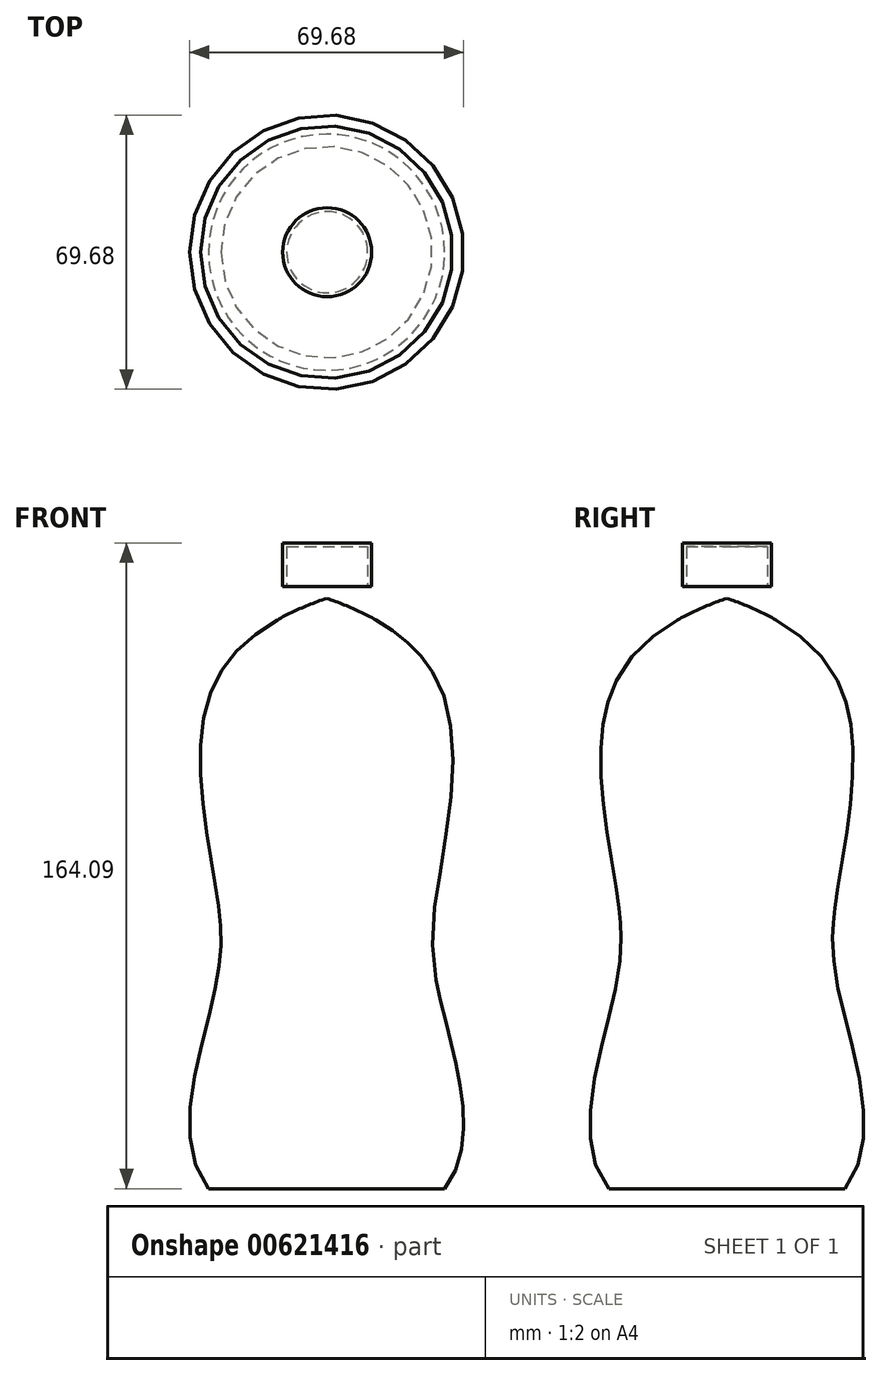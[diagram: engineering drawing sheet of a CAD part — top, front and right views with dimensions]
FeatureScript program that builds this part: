
annotation { "Feature Type Name" : "Feature", "Feature Type Description" : "" }
export const myFeature = defineFeature(function(context is Context, id is Id, definition is map)
    precondition{}
    {
        {
            var Q0;
            Q0=qCreatedBy(makeId("Front.planeOp"),FACE);
            var sketch = newSketch(context, id + "F0", { "sketchPlane" : qUnion([Q0])});
            skLineSegment(sketch, "E0", {"start": v(0, 0) * mm, "end": v(-30, 0) * mm});
            skLineSegment(sketch, "E1", {"start": v(0, 0) * mm, "end": v(0, 150) * mm});
            skFitSpline(sketch, "E2", {"points": [v(-30, 0) * mm, v(-28.38, 50.35) * mm, v(-28.38, 77.8) * mm, v(-30, 124.48) * mm, v(0, 150) * mm], "startDerivative": vector(-110.1, 134.52) * mm, "endDerivative": vector(179.2, 61.1) * mm});
            skLineSegment(sketch, "E3", {"start": v(-10, 148.83) * mm, "end": v(-10, 162.94) * mm});
            skLineSegment(sketch, "E4", {"start": v(-10, 162.94) * mm, "end": v(0, 162.94) * mm});
            skLineSegment(sketch, "E5", {"start": v(0, 162.94) * mm, "end": v(0, 150) * mm});
            skPoint(sketch, "E6.visualSharp", {"position": v(-10, 145.84) * mm});
            skArc(sketch, "E6.filletArc", {"start": v(-12.53, 144.49) * mm, "mid": v(-10.68, 146.32) * mm, "end": v(-10, 148.83) * mm});
            skLineSegment(sketch, "E7.0", {"start": v(-10.15, 152.94) * mm, "end": v(-10.15, 162.94) * mm});
            skLineSegment(sketch, "E8", {"start": v(-11.15, 152.94) * mm, "end": v(-11.15, 162.94) * mm});
            skLineSegment(sketch, "E9", {"start": v(-11.15, 152.94) * mm, "end": v(-10.15, 152.94) * mm});
            skLineSegment(sketch, "E10", {"start": v(-10.15, 162.94) * mm, "end": v(-10, 162.94) * mm, "construction": true});
            skLineSegment(sketch, "E11", {"start": v(-5, 162.94) * mm, "end": v(-5, 159.67) * mm, "construction": true});
            skLineSegment(sketch, "E12.MirrorCS", {"start": v(1.15, 152.94) * mm, "end": v(1.15, 162.94) * mm});
            skLineSegment(sketch, "E13.MirrorCS", {"start": v(0.15, 152.94) * mm, "end": v(0.15, 162.94) * mm});
            skLineSegment(sketch, "E14.MirrorCS", {"start": v(1.15, 152.94) * mm, "end": v(0.15, 152.94) * mm});
            skLineSegment(sketch, "E15", {"start": v(-10.15, 163.09) * mm, "end": v(0.15, 163.09) * mm});
            skLineSegment(sketch, "E16", {"start": v(-10.15, 162.94) * mm, "end": v(-10.15, 163.09) * mm});
            skLineSegment(sketch, "E17", {"start": v(0.15, 162.94) * mm, "end": v(0.15, 163.09) * mm});
            skLineSegment(sketch, "E18", {"start": v(1.15, 162.94) * mm, "end": v(1.15, 163.09) * mm});
            skLineSegment(sketch, "E19", {"start": v(-11.15, 162.94) * mm, "end": v(-11.15, 163.09) * mm});
            skLineSegment(sketch, "E20", {"start": v(-11.15, 164.09) * mm, "end": v(1.15, 164.09) * mm});
            skLineSegment(sketch, "E21", {"start": v(-11.15, 163.09) * mm, "end": v(-11.15, 164.09) * mm});
            skLineSegment(sketch, "E22", {"start": v(1.15, 164.09) * mm, "end": v(1.15, 163.09) * mm});
            skLineSegment(sketch, "E23", {"start": v(-5, 163.09) * mm, "end": v(-5, 164.09) * mm});
            skLineSegment(sketch, "E24", {"start": v(0.15, 163.09) * mm, "end": v(0.15, 164.09) * mm});
            skSolve(sketch);
        }
        {
            var Q0;
            Q0=makeQuery(id+"F0.imprint","IMPRINT",FACE,{"disambiguationData":[TD([[makeQuery(id+"F0.imprint","IMPRINT",EDGE,{"derivedFrom":sQuery(id+"F0.wireOp",EDGE,"E0")}),-1.0]])]});
            var Q1;
            Q1=sQuery(id+"F0.wireOp",EDGE,"E1");
            revolve(context, id + "F1", {"entities" : qUnion([Q0]), "axis" : qUnion([Q1]), "revolveType" : RevolveType.FULL});
        }
        {
            var Q0;
            Q0=makeQuery(id+"F0.imprint","IMPRINT",FACE,{"disambiguationData":[TD([[makeQuery(id+"F0.imprint","IMPRINT",EDGE,{"derivedFrom":sQuery(id+"F0.wireOp",EDGE,"E7.0")}),1.0]])]});
            var Q1;
            {var subQ2=sQuery(id+"F0.wireOp",EDGE,"E23");Q1=makeQuery(id+"F0.imprint","IMPRINT",FACE,{"disambiguationData":[TD([[makeQuery(id+"F0.imprint","IMPRINT",EDGE,{"derivedFrom":subQ2}),-1.0]])]});}
            var Q2;
            Q2=sQuery(id+"F0.wireOp",EDGE,"E24");
            revolve(context, id + "F2", {"entities" : qUnion([Q0, Q1]), "axis" : qUnion([Q2]), "revolveType" : RevolveType.FULL});
        }
    });
